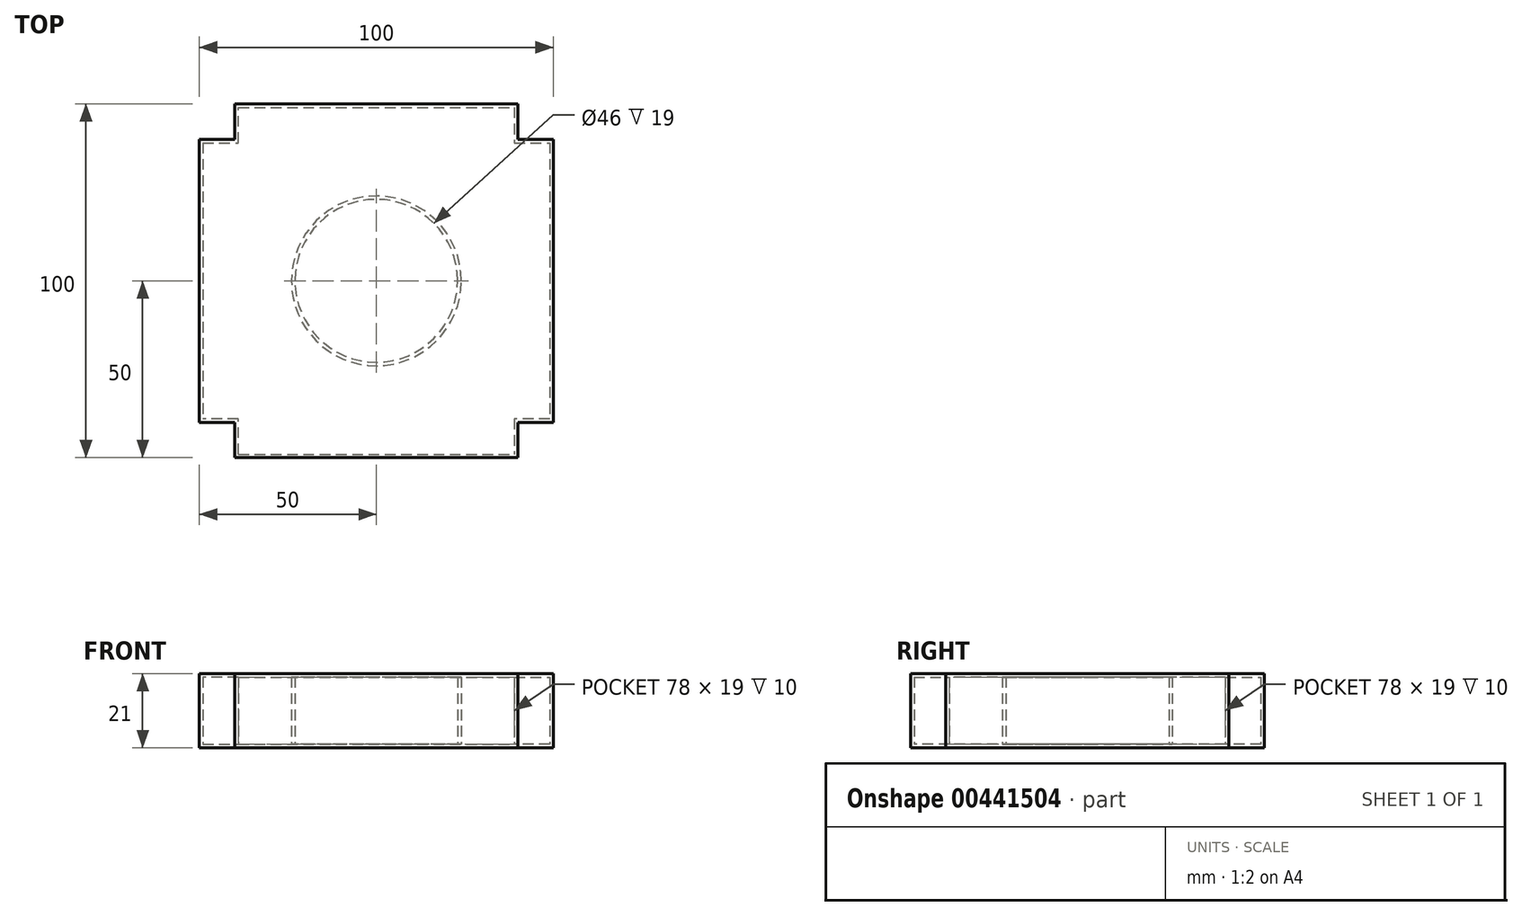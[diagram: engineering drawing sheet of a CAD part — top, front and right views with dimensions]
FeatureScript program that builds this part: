
annotation { "Feature Type Name" : "Feature", "Feature Type Description" : "" }
export const myFeature = defineFeature(function(context is Context, id is Id, definition is map)
    precondition{}
    {
        {
            var Q0;
            Q0=qCreatedBy(makeId("Top.planeOp"),FACE);
            var sketch = newSketch(context, id + "F0", { "sketchPlane" : qUnion([Q0])});
            skLineSegment(sketch, "E0.bottom", {"start": v(-40, 50) * mm, "end": v(40, 50) * mm});
            skLineSegment(sketch, "E0.top", {"start": v(-40, -50) * mm, "end": v(40, -50) * mm});
            skLineSegment(sketch, "E0.left", {"start": v(-50, 40) * mm, "end": v(-50, -40) * mm});
            skLineSegment(sketch, "E0.right", {"start": v(50, 40) * mm, "end": v(50, -40) * mm});
            skLineSegment(sketch, "E1", {"start": v(-50, 40) * mm, "end": v(-40, 40) * mm});
            skLineSegment(sketch, "E2", {"start": v(-40, 40) * mm, "end": v(-40, 50) * mm});
            skLineSegment(sketch, "E3.1.0", {"start": v(-40, -50) * mm, "end": v(-40, -40) * mm});
            skLineSegment(sketch, "E3.1.1", {"start": v(-40, -40) * mm, "end": v(-50, -40) * mm});
            skLineSegment(sketch, "E3.2.0", {"start": v(50, -40) * mm, "end": v(40, -40) * mm});
            skLineSegment(sketch, "E3.2.1", {"start": v(40, -40) * mm, "end": v(40, -50) * mm});
            skLineSegment(sketch, "E3.3.0", {"start": v(40, 50) * mm, "end": v(40, 40) * mm});
            skLineSegment(sketch, "E3.3.1", {"start": v(40, 40) * mm, "end": v(50, 40) * mm});
            skPoint(sketch, "E3.center", {"position": v(0, 0) * mm});
            skSolve(sketch);
        }
        {
            var Q0;
            Q0=makeQuery(id+"F0.imprint","IMPRINT",FACE,{"disambiguationData":[TD([[makeQuery(id+"F0.imprint","IMPRINT",EDGE,{"derivedFrom":sQuery(id+"F0.wireOp",EDGE,"E0.bottom")}),-1.0]])]});
            extrude(context, id + "F1", {"entities" : qUnion([Q0]), "depth" : 20 * mm});
        }
        {
            var Q0;
            Q0=makeQuery(id+"F1.opExtrude","CAP_FACE",FACE,{"disambiguationData":[OSD([sQuery(id+"F0.wireOp",EDGE,"E0.bottom"),sQuery(id+"F0.wireOp",EDGE,"E0.top"),sQuery(id+"F0.wireOp",EDGE,"E0.left"),sQuery(id+"F0.wireOp",EDGE,"E0.right")])],"isStart":false});
            shell(context, id + "F2", {"entities" : qUnion([Q0]), "thickness" : 1 * mm});
        }
        {
            var Q0;
            Q0=makeQuery(id+"F2.opShell","OFFSET_FACE",FACE,{"disambiguationData":[OSD([sQuery(id+"F0.wireOp",EDGE,"E0.bottom"),sQuery(id+"F0.wireOp",EDGE,"E0.top"),sQuery(id+"F0.wireOp",EDGE,"E0.left"),sQuery(id+"F0.wireOp",EDGE,"E0.right")])]});
            var sketch = newSketch(context, id + "F3", { "sketchPlane" : qUnion([Q0])});
            skCircle(sketch, "E4", {"center": v(0, 0) * mm, "radius": 24 * mm});
            skSolve(sketch);
        }
        {
            var Q0;
            Q0=makeQuery(id+"F3.imprint","IMPRINT",FACE,{"disambiguationData":[TD([[makeQuery(id+"F3.imprint","IMPRINT",EDGE,{"derivedFrom":sQuery(id+"F3.wireOp",EDGE,"E4")}),1.0]])]});
            extrude(context, id + "F4", {"entities" : qUnion([Q0]), "operationType" : NewBodyOperationType.ADD, "depth" : 19 * mm});
        }
        {
            var Q0;
            Q0=makeQuery(id+"F4.opExtrude","CAP_FACE",FACE,{"disambiguationData":[OSD([sQuery(id+"F3.wireOp",EDGE,"E4")])],"isStart":false});
            shell(context, id + "F5", {"entities" : qUnion([Q0]), "thickness" : 1 * mm});
        }
        {
            var Q0;
            Q0=makeQuery(id+"F1.opExtrude","CAP_FACE",FACE,{"disambiguationData":[OSD([sQuery(id+"F0.wireOp",EDGE,"E0.bottom"),sQuery(id+"F0.wireOp",EDGE,"E0.top"),sQuery(id+"F0.wireOp",EDGE,"E0.left"),sQuery(id+"F0.wireOp",EDGE,"E0.right")])],"isStart":false});
            var sketch = newSketch(context, id + "F6", { "sketchPlane" : qUnion([Q0])});
            skLineSegment(sketch, "E5.bottom", {"start": v(40, -50) * mm, "end": v(-40, -50) * mm});
            skLineSegment(sketch, "E5.top", {"start": v(40, 50) * mm, "end": v(-40, 50) * mm});
            skLineSegment(sketch, "E5.left", {"start": v(50, -40) * mm, "end": v(50, 40) * mm});
            skLineSegment(sketch, "E5.right", {"start": v(-50, -40) * mm, "end": v(-50, 40) * mm});
            skLineSegment(sketch, "E6", {"start": v(-50, 40) * mm, "end": v(-40, 40) * mm});
            skLineSegment(sketch, "E7", {"start": v(-40, 40) * mm, "end": v(-40, 50) * mm});
            skLineSegment(sketch, "E8.1.0", {"start": v(-40, -50) * mm, "end": v(-40, -40) * mm});
            skLineSegment(sketch, "E8.1.1", {"start": v(-40, -40) * mm, "end": v(-50, -40) * mm});
            skLineSegment(sketch, "E8.2.0", {"start": v(50, -40) * mm, "end": v(40, -40) * mm});
            skLineSegment(sketch, "E8.2.1", {"start": v(40, -40) * mm, "end": v(40, -50) * mm});
            skLineSegment(sketch, "E8.3.0", {"start": v(40, 50) * mm, "end": v(40, 40) * mm});
            skLineSegment(sketch, "E8.3.1", {"start": v(40, 40) * mm, "end": v(50, 40) * mm});
            skPoint(sketch, "E8.center", {"position": v(0, 0) * mm});
            skSolve(sketch);
        }
        {
            var Q0;
            Q0 = qSketchRegion(id + "F6", true);
            extrude(context, id + "F7", {"entities" : qUnion([Q0]), "operationType" : NewBodyOperationType.ADD, "depth" : 1 * mm});
        }
    });
